# Revit family: DC_Rheem_PLM_Raypak_B3164ID
name_source: partatom
category: Plumbing Fixtures
revit_build: Autodesk Revit 2017 (Build: 20160225_1515(x64)
units: mm (PartAtom-declared; Revit-internal decimal feet)

## family parameters
Cut with Voids When Loaded = No
Host = Face
Part Type = Normal
Room Calculation Point = No
Round Connector Dimension = Use Radius
Shared = No

## types (4) — shared parameters
ColdWaterPipeDiameter_ANZRS = 80 mm  [stored 0.262467 ft]
ColdWaterRadius_ANZRS = 40 mm  [stored 0.131234 ft]
Height_ANZRS = 1738 mm
HotWaterPipeDiameter_ANZRS = 80 mm  [stored 0.262467 ft]
HotWaterRadius_ANZRS = 40 mm  [stored 0.131234 ft]
Manufacturer = Raypak
PRVR_ANZRS = 20 mm  [stored 0.0656168 ft]
Stainless Steel = Raypak - Grey Powder Coated Steel
TopDiameter_ANZRS = 710 mm
TopWidth_ANZRS = 1445 mm
URL = http://www.rheem.com.au
Width_ANZRS = 2060 mm  [stored 6.75853 ft]

## per-type parameters (varying)
| type | Default Elevation | GasOutletRadius_ANZRS | GasPipeDiameter_ANZRS | Model | Type Comments |
| Raypak - Gas Water Heater- Indoor - 3165 MJ/h  Natural gas, modulating gas control | 1219 mm | 33 mm | 65 mm  [stored 0.213255 ft] | B3164NCM/ID | Recovery 12384L/h @ 50°C rise |
| Raypak - Gas Water Heater- Indoor - 3165 MJ/h  Natural gas, On/Off gas control | 1219 mm | 33 mm | 65 mm  [stored 0.213255 ft] | B3164NCO/ID | Recovery 12384L/h @ 50°C rise |
| Raypak - Gas Water Heater- Indoor - 3035 MJ/h  Propane gas, modulating gas control | 1219 mm | 20 mm  [stored 0.0656168 ft] | 40 mm  [stored 0.131234 ft] | B3164PCM/ID | Recovery 11610L/h @ 50°C rise |
| Raypak - Gas Water Heater- Indoor - 3035 MJ/h  Propane gas, On/Off gas control | 0 mm  [stored 0 ft] | 20 mm  [stored 0.0656168 ft] | 40 mm  [stored 0.131234 ft] | B3164PCO/ID | Recovery 11610L/h @ 50°C rise |

note: column(s) folded — value = type name in every type: Description

note: [stored X ft] marks values corroborated as IEEE doubles in the binary element streams (Revit-internal decimal feet)

## geometry (parser evidence)
native form markers: Blend x6, Sweep x3
no freeform markers — native parametric forms only
